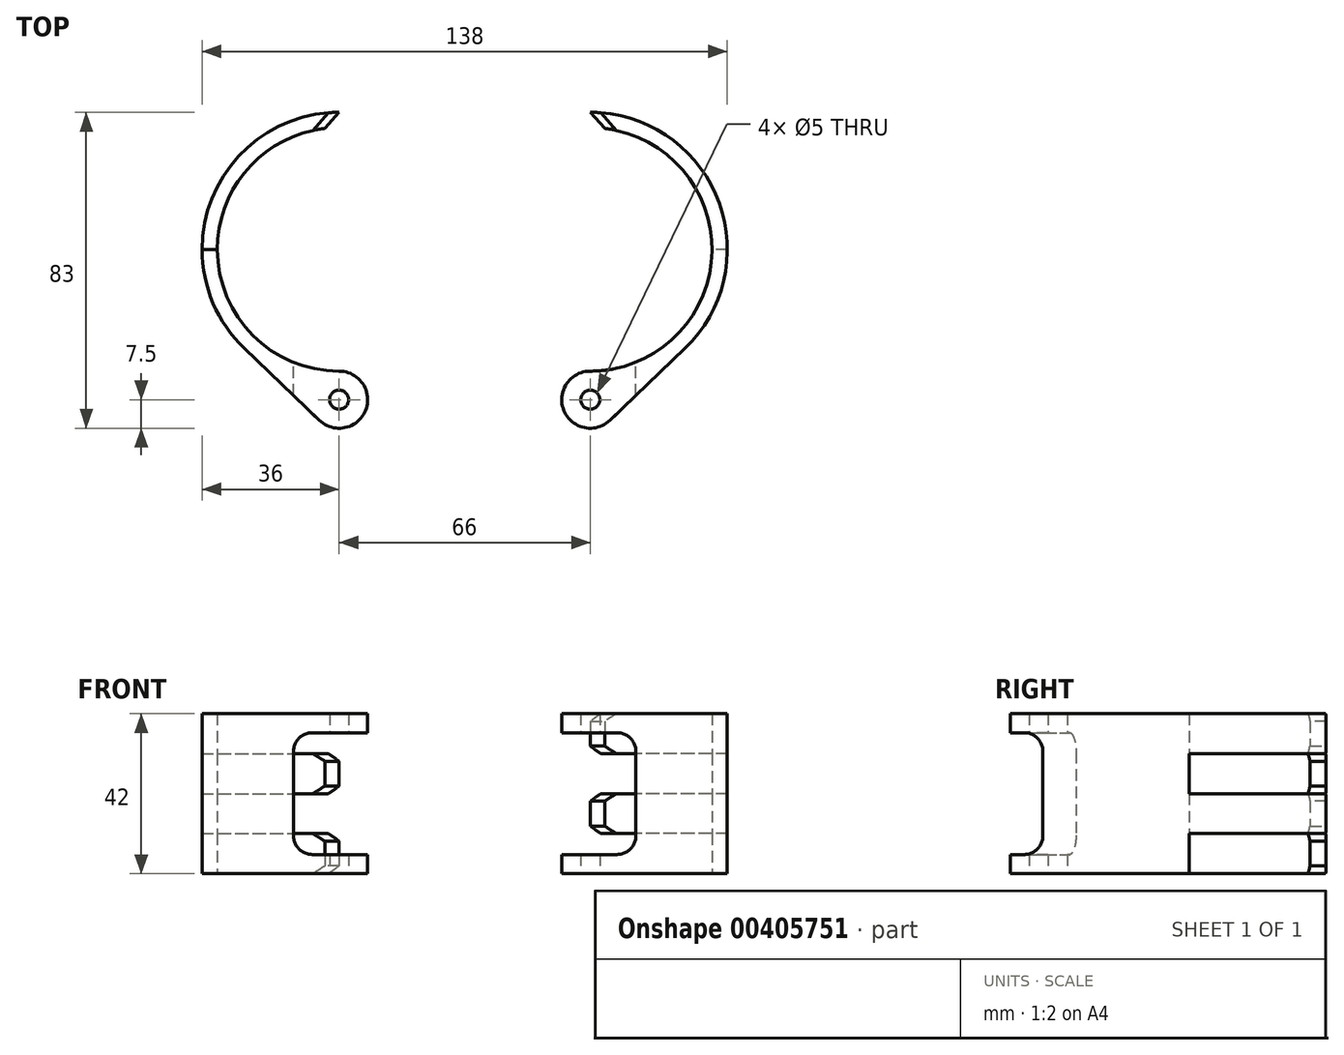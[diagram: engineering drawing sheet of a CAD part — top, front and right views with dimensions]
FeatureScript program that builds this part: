
annotation { "Feature Type Name" : "Feature", "Feature Type Description" : "" }
export const myFeature = defineFeature(function(context is Context, id is Id, definition is map)
    precondition{}
    {
        {
            var Q0;
            Q0=qCreatedBy(makeId("Top.planeOp"),FACE);
            var sketch = newSketch(context, id + "F0", { "sketchPlane" : qUnion([Q0])});
            skLineSegment(sketch, "E0", {"start": v(-33, 0) * mm, "end": v(33, 0) * mm, "construction": true});
            skPoint(sketch, "E1", {"position": v(0, 0) * mm});
            skCircle(sketch, "E2", {"center": v(-33, 0) * mm, "radius": 32 * mm});
            skCircle(sketch, "E3", {"center": v(33, 0) * mm, "radius": 32 * mm});
            skCircle(sketch, "E4", {"center": v(-33, 0) * mm, "radius": 36 * mm});
            skCircle(sketch, "E5", {"center": v(33, 0) * mm, "radius": 36 * mm});
            skCircle(sketch, "E6", {"center": v(-33, -39.5) * mm, "radius": 7.5 * mm});
            skCircle(sketch, "E7", {"center": v(33, -39.5) * mm, "radius": 7.5 * mm});
            skLineSegment(sketch, "E8", {"start": v(-38.2, -44.91) * mm, "end": v(-57.93, -25.97) * mm});
            skLineSegment(sketch, "E9", {"start": v(38.2, -44.91) * mm, "end": v(57.93, -25.97) * mm});
            skLineSegment(sketch, "E10", {"start": v(-33, 0) * mm, "end": v(-33, 36) * mm});
            skLineSegment(sketch, "E11", {"start": v(33, 0) * mm, "end": v(33, 36) * mm});
            skCircle(sketch, "E12", {"center": v(-33, -39.5) * mm, "radius": 2.5 * mm});
            skCircle(sketch, "E13", {"center": v(33, -39.5) * mm, "radius": 2.5 * mm});
            skLineSegment(sketch, "E14", {"start": v(-33, -39.5) * mm, "end": v(33, -39.5) * mm});
            skLineSegment(sketch, "E15", {"start": v(-33, 0) * mm, "end": v(-33, -39.5) * mm});
            skLineSegment(sketch, "E16", {"start": v(33, 0) * mm, "end": v(33, -39.5) * mm});
            skSolve(sketch);
        }
        {
            var Q0;
            {var subQ0=sQuery(id+"F0.wireOp",EDGE,"E6");var subQ1=sQuery(id+"F0.wireOp",EDGE,"E4");var subQ2=makeQuery(id+"F0.imprint","INTERSECT",VERTEX,{"disambiguationData":[OD(0.0)],"derivedFrom":[subQ1,subQ0]});Q0=makeQuery(id+"F0.imprint","IMPRINT",FACE,{"disambiguationData":[TD([[makeQuery(id+"F0.imprint","IMPRINT",EDGE,{"disambiguationData":[TD([[subQ2,1.0]])],"derivedFrom":subQ1}),-1.0]])]});}
            var Q1;
            {var subQ0=sQuery(id+"F0.wireOp",EDGE,"E6");var subQ1=sQuery(id+"F0.wireOp",EDGE,"E4");var subQ2=makeQuery(id+"F0.imprint","INTERSECT",VERTEX,{"disambiguationData":[OD(0.0)],"derivedFrom":[subQ1,subQ0]});Q1=makeQuery(id+"F0.imprint","IMPRINT",FACE,{"disambiguationData":[TD([[makeQuery(id+"F0.imprint","IMPRINT",EDGE,{"disambiguationData":[TD([[subQ2,1.0]])],"derivedFrom":subQ1}),1.0]])]});}
            var Q2;
            {var subQ0=sQuery(id+"F0.wireOp",EDGE,"E8");Q2=makeQuery(id+"F0.imprint","IMPRINT",FACE,{"disambiguationData":[TD([[makeQuery(id+"F0.imprint","IMPRINT",EDGE,{"derivedFrom":subQ0}),-1.0]])]});}
            var Q3;
            {var subQ0=sQuery(id+"F0.wireOp",EDGE,"E7");var subQ1=sQuery(id+"F0.wireOp",EDGE,"E5");var subQ2=makeQuery(id+"F0.imprint","INTERSECT",VERTEX,{"disambiguationData":[OD(0.0)],"derivedFrom":[subQ1,subQ0]});Q3=makeQuery(id+"F0.imprint","IMPRINT",FACE,{"disambiguationData":[TD([[makeQuery(id+"F0.imprint","IMPRINT",EDGE,{"disambiguationData":[TD([[subQ2,-1.0]])],"derivedFrom":subQ1}),-1.0]])]});}
            var Q4;
            {var subQ0=sQuery(id+"F0.wireOp",EDGE,"E9");Q4=makeQuery(id+"F0.imprint","IMPRINT",FACE,{"disambiguationData":[TD([[makeQuery(id+"F0.imprint","IMPRINT",EDGE,{"derivedFrom":subQ0}),1.0]])]});}
            var Q5;
            {var subQ0=sQuery(id+"F0.wireOp",EDGE,"E7");var subQ1=sQuery(id+"F0.wireOp",EDGE,"E5");var subQ2=makeQuery(id+"F0.imprint","INTERSECT",VERTEX,{"disambiguationData":[OD(0.0)],"derivedFrom":[subQ1,subQ0]});Q5=makeQuery(id+"F0.imprint","IMPRINT",FACE,{"disambiguationData":[TD([[makeQuery(id+"F0.imprint","IMPRINT",EDGE,{"disambiguationData":[TD([[subQ2,-1.0]])],"derivedFrom":subQ1}),1.0]])]});}
            var Q6;
            {var subQ1=sQuery(id+"F0.wireOp",EDGE,"E3");var subQ6=sQuery(id+"F0.wireOp",EDGE,"E11");var subQ8=makeQuery(id+"F0.imprint","INTERSECT",VERTEX,{"derivedFrom":[subQ1,subQ6]});Q6=makeQuery(id+"F0.imprint","IMPRINT",FACE,{"disambiguationData":[TD([[makeQuery(id+"F0.imprint","IMPRINT",EDGE,{"disambiguationData":[TD([[subQ8,1.0]])],"derivedFrom":subQ1}),-1.0]])]});}
            var Q7;
            {var subQ1=sQuery(id+"F0.wireOp",EDGE,"E2");var subQ6=sQuery(id+"F0.wireOp",EDGE,"E10");var subQ8=makeQuery(id+"F0.imprint","INTERSECT",VERTEX,{"derivedFrom":[subQ1,subQ6]});Q7=makeQuery(id+"F0.imprint","IMPRINT",FACE,{"disambiguationData":[TD([[makeQuery(id+"F0.imprint","IMPRINT",EDGE,{"disambiguationData":[TD([[subQ8,-1.0]])],"derivedFrom":subQ1}),-1.0]])]});}
            var Q8;
            Q8=makeQuery(id+"F0.imprint","IMPRINT",FACE,{"disambiguationData":[TD([[makeQuery(id+"F0.imprint","IMPRINT",EDGE,{"derivedFrom":sQuery(id+"F0.wireOp",EDGE,"E12")}),-1.0]])]});
            var Q9;
            {var subQ0=sQuery(id+"F0.wireOp",EDGE,"E6");var subQ1=sQuery(id+"F0.wireOp",EDGE,"E4");var subQ2=makeQuery(id+"F0.imprint","INTERSECT",VERTEX,{"disambiguationData":[OD(0.0)],"derivedFrom":[subQ1,subQ0]});Q9=makeQuery(id+"F0.imprint","IMPRINT",FACE,{"disambiguationData":[TD([[makeQuery(id+"F0.imprint","IMPRINT",EDGE,{"disambiguationData":[TD([[subQ2,-1.0]])],"derivedFrom":subQ1}),1.0]])]});}
            var Q10;
            {var subQ0=sQuery(id+"F0.wireOp",EDGE,"E15");var subQ1=sQuery(id+"F0.wireOp",EDGE,"E4");var subQ2=makeQuery(id+"F0.imprint","INTERSECT",VERTEX,{"derivedFrom":[subQ1,subQ0]});Q10=makeQuery(id+"F0.imprint","IMPRINT",FACE,{"disambiguationData":[TD([[makeQuery(id+"F0.imprint","IMPRINT",EDGE,{"disambiguationData":[TD([[subQ2,-1.0]])],"derivedFrom":subQ1}),1.0]])]});}
            var Q11;
            {var subQ5=sQuery(id+"F0.wireOp",EDGE,"E6");var subQ8=sQuery(id+"F0.wireOp",EDGE,"E4");var subQ9=makeQuery(id+"F0.imprint","INTERSECT",VERTEX,{"disambiguationData":[OD(0.0)],"derivedFrom":[subQ8,subQ5]});Q11=makeQuery(id+"F0.imprint","IMPRINT",FACE,{"disambiguationData":[TD([[makeQuery(id+"F0.imprint","IMPRINT",EDGE,{"disambiguationData":[TD([[subQ9,-1.0]])],"derivedFrom":subQ8}),-1.0]])]});}
            var Q12;
            {var subQ3=sQuery(id+"F0.wireOp",EDGE,"E16");var subQ8=sQuery(id+"F0.wireOp",EDGE,"E5");var subQ9=makeQuery(id+"F0.imprint","INTERSECT",VERTEX,{"derivedFrom":[subQ8,subQ3]});Q12=makeQuery(id+"F0.imprint","IMPRINT",FACE,{"disambiguationData":[TD([[makeQuery(id+"F0.imprint","IMPRINT",EDGE,{"disambiguationData":[TD([[subQ9,-1.0]])],"derivedFrom":subQ8}),-1.0]])]});}
            var Q13;
            {var subQ0=sQuery(id+"F0.wireOp",EDGE,"E16");var subQ1=sQuery(id+"F0.wireOp",EDGE,"E5");var subQ2=makeQuery(id+"F0.imprint","INTERSECT",VERTEX,{"derivedFrom":[subQ1,subQ0]});Q13=makeQuery(id+"F0.imprint","IMPRINT",FACE,{"disambiguationData":[TD([[makeQuery(id+"F0.imprint","IMPRINT",EDGE,{"disambiguationData":[TD([[subQ2,-1.0]])],"derivedFrom":subQ1}),1.0]])]});}
            extrude(context, id + "F1", {"entities" : qUnion([Q0, Q1, Q2, Q3, Q4, Q5, Q6, Q7, Q8, Q9, Q10, Q11, Q12, Q13]), "endBound" : BoundingType.SYMMETRIC, "depth" : 42 * mm});
        }
        {
            var Q0;
            Q0=qCreatedBy(makeId("Front.planeOp"),FACE);
            var sketch = newSketch(context, id + "F2", { "sketchPlane" : qUnion([Q0])});
            skLineSegment(sketch, "E17.bottom", {"start": v(-45, 16) * mm, "end": v(45, 16) * mm});
            skLineSegment(sketch, "E17.top", {"start": v(-45, -16) * mm, "end": v(45, -16) * mm});
            skLineSegment(sketch, "E17.left", {"start": v(-45, 16) * mm, "end": v(-45, -16) * mm});
            skLineSegment(sketch, "E17.right", {"start": v(45, 16) * mm, "end": v(45, -16) * mm});
            skLineSegment(sketch, "E18", {"start": v(-45, 16) * mm, "end": v(45, -16) * mm, "construction": true});
            skPoint(sketch, "E19", {"position": v(0, 0) * mm});
            skSolve(sketch);
        }
        {
            var Q0;
            Q0=makeQuery(id+"F2.imprint","IMPRINT",FACE,{"disambiguationData":[TD([[makeQuery(id+"F2.imprint","IMPRINT",EDGE,{"derivedFrom":sQuery(id+"F2.wireOp",EDGE,"E17.bottom")}),-1.0]])]});
            var Q1;
            Q1=makeQuery(id+"F1.opExtrude","CAP_VERTEX",VERTEX,{"disambiguationData":[OSD([sQuery(id+"F0.wireOp",EDGE,"E6"),sQuery(id+"F0.wireOp",EDGE,"E8")])],"isStart":false});
            extrude(context, id + "F3", {"entities" : qUnion([Q0]), "operationType" : NewBodyOperationType.REMOVE, "endBoundEntityVertex" : qUnion([Q1]), "depth" : 60 * mm});
        }
        {
            var Q0;
            Q0=makeQuery(id+"F3.boolean.opBoolean","COPY",EDGE,{"derivedFrom":makeQuery(id+"F3.opExtrude","SWEPT_EDGE",EDGE,{"disambiguationData":[OSD([sQuery(id+"F2.wireOp",EDGE,"E17.bottom"),sQuery(id+"F2.wireOp",EDGE,"E17.right")])]})});
            var Q1;
            Q1=makeQuery(id+"F3.boolean.opBoolean","COPY",EDGE,{"derivedFrom":makeQuery(id+"F3.opExtrude","SWEPT_EDGE",EDGE,{"disambiguationData":[OSD([sQuery(id+"F2.wireOp",EDGE,"E17.top"),sQuery(id+"F2.wireOp",EDGE,"E17.right")])]})});
            var Q2;
            Q2=makeQuery(id+"F3.boolean.opBoolean","COPY",EDGE,{"derivedFrom":makeQuery(id+"F3.opExtrude","SWEPT_EDGE",EDGE,{"disambiguationData":[OSD([sQuery(id+"F2.wireOp",EDGE,"E17.bottom"),sQuery(id+"F2.wireOp",EDGE,"E17.left")])]})});
            var Q3;
            Q3=makeQuery(id+"F3.boolean.opBoolean","COPY",EDGE,{"derivedFrom":makeQuery(id+"F3.opExtrude","SWEPT_EDGE",EDGE,{"disambiguationData":[OSD([sQuery(id+"F2.wireOp",EDGE,"E17.top"),sQuery(id+"F2.wireOp",EDGE,"E17.left")])]})});
            fillet(context, id + "F4", {"entities" : qUnion([Q0, Q1, Q2, Q3]), "radius" : 5 * mm, "tangentPropagation" : true, "allowEdgeOverflow" : false});
        }
        {
            var Q0;
            Q0=qCreatedBy(makeId("Right.planeOp"),FACE);
            var sketch = newSketch(context, id + "F5", { "sketchPlane" : qUnion([Q0])});
            skLineSegment(sketch, "E20.bottom", {"start": v(0, 0) * mm, "end": v(36, 0) * mm});
            skLineSegment(sketch, "E20.top", {"start": v(0, 10.5) * mm, "end": v(36, 10.5) * mm});
            skLineSegment(sketch, "E20.left", {"start": v(0, 0) * mm, "end": v(0, 10.5) * mm});
            skLineSegment(sketch, "E20.right", {"start": v(36, 0) * mm, "end": v(36, 10.5) * mm});
            skLineSegment(sketch, "E21.top", {"start": v(0, 21) * mm, "end": v(36, 21) * mm});
            skLineSegment(sketch, "E21.left", {"start": v(0, 10.5) * mm, "end": v(0, 21) * mm});
            skLineSegment(sketch, "E21.right", {"start": v(36, 10.5) * mm, "end": v(36, 21) * mm});
            skLineSegment(sketch, "E22.top", {"start": v(0, -10.5) * mm, "end": v(36, -10.5) * mm});
            skLineSegment(sketch, "E22.left", {"start": v(0, 0) * mm, "end": v(0, -10.5) * mm});
            skLineSegment(sketch, "E22.right", {"start": v(36, 0) * mm, "end": v(36, -10.5) * mm});
            skLineSegment(sketch, "E23.top", {"start": v(0, -21) * mm, "end": v(36, -21) * mm});
            skLineSegment(sketch, "E23.left", {"start": v(0, -10.5) * mm, "end": v(0, -21) * mm});
            skLineSegment(sketch, "E23.right", {"start": v(36, -10.5) * mm, "end": v(36, -21) * mm});
            skSolve(sketch);
        }
        {
            var Q0;
            Q0=makeQuery(id+"F5.imprint","IMPRINT",FACE,{"disambiguationData":[TD([[makeQuery(id+"F5.imprint","IMPRINT",EDGE,{"derivedFrom":sQuery(id+"F5.wireOp",EDGE,"E20.top")}),1.0]])]});
            var Q1;
            Q1=makeQuery(id+"F5.imprint","IMPRINT",FACE,{"disambiguationData":[TD([[makeQuery(id+"F5.imprint","IMPRINT",EDGE,{"derivedFrom":sQuery(id+"F5.wireOp",EDGE,"E20.bottom")}),-1.0]])]});
            extrude(context, id + "F6", {"entities" : qUnion([Q0, Q1]), "operationType" : NewBodyOperationType.REMOVE, "oppositeDirection" : true, "depth" : 80 * mm});
        }
        {
            var Q0;
            Q0=qCreatedBy(makeId("Right.planeOp"),FACE);
            var sketch = newSketch(context, id + "F7", { "sketchPlane" : qUnion([Q0])});
            skLineSegment(sketch, "E24.bottom", {"start": v(0, 0) * mm, "end": v(36, 0) * mm});
            skLineSegment(sketch, "E24.top", {"start": v(0, 10.5) * mm, "end": v(36, 10.5) * mm});
            skLineSegment(sketch, "E24.left", {"start": v(0, 0) * mm, "end": v(0, 10.5) * mm});
            skLineSegment(sketch, "E24.right", {"start": v(36, 0) * mm, "end": v(36, 10.5) * mm});
            skLineSegment(sketch, "E25.top", {"start": v(0, 21) * mm, "end": v(36, 21) * mm});
            skLineSegment(sketch, "E25.left", {"start": v(0, 10.5) * mm, "end": v(0, 21) * mm});
            skLineSegment(sketch, "E25.right", {"start": v(36, 10.5) * mm, "end": v(36, 21) * mm});
            skLineSegment(sketch, "E26.top", {"start": v(0, -10.5) * mm, "end": v(36, -10.5) * mm});
            skLineSegment(sketch, "E26.left", {"start": v(0, 0) * mm, "end": v(0, -10.5) * mm});
            skLineSegment(sketch, "E26.right", {"start": v(36, 0) * mm, "end": v(36, -10.5) * mm});
            skLineSegment(sketch, "E27.top", {"start": v(0, -21) * mm, "end": v(36, -21) * mm});
            skLineSegment(sketch, "E27.left", {"start": v(0, -10.5) * mm, "end": v(0, -21) * mm});
            skLineSegment(sketch, "E27.right", {"start": v(36, -10.5) * mm, "end": v(36, -21) * mm});
            skSolve(sketch);
        }
        {
            var Q0;
            Q0=makeQuery(id+"F7.imprint","IMPRINT",FACE,{"disambiguationData":[TD([[makeQuery(id+"F7.imprint","IMPRINT",EDGE,{"derivedFrom":sQuery(id+"F7.wireOp",EDGE,"E24.left")}),-1.0]])]});
            var Q1;
            Q1=makeQuery(id+"F7.imprint","IMPRINT",FACE,{"disambiguationData":[TD([[makeQuery(id+"F7.imprint","IMPRINT",EDGE,{"derivedFrom":sQuery(id+"F7.wireOp",EDGE,"E26.top")}),-1.0]])]});
            extrude(context, id + "F8", {"entities" : qUnion([Q0, Q1]), "operationType" : NewBodyOperationType.REMOVE, "depth" : 80 * mm});
        }
        {
            var Q0;
            {var subQ0=sQuery(id+"F0.wireOp",EDGE,"E2");var subQ1=sQuery(id+"F0.wireOp",EDGE,"E10");Q0=makeQuery(id+"F6.boolean.opBoolean","SPLIT",EDGE,{"disambiguationData":[TD([makeQuery(id+"F6.opExtrude","SWEPT_FACE",FACE,{"disambiguationData":[OSD([sQuery(id+"F5.wireOp",EDGE,"E20.top")])]})])],"derivedFrom":makeQuery(id+"F1.opExtrude","SWEPT_EDGE",EDGE,{"disambiguationData":[OSD([subQ0,subQ1])]})});}
            var Q1;
            {var subQ0=sQuery(id+"F0.wireOp",EDGE,"E2");var subQ1=sQuery(id+"F0.wireOp",EDGE,"E10");Q1=makeQuery(id+"F6.boolean.opBoolean","SPLIT",EDGE,{"disambiguationData":[TD([makeQuery(id+"F6.opExtrude","SWEPT_FACE",FACE,{"disambiguationData":[OSD([sQuery(id+"F5.wireOp",EDGE,"E22.top")])]})])],"derivedFrom":makeQuery(id+"F1.opExtrude","SWEPT_EDGE",EDGE,{"disambiguationData":[OSD([subQ0,subQ1])]})});}
            var Q2;
            {var subQ0=sQuery(id+"F0.wireOp",EDGE,"E3");var subQ1=sQuery(id+"F0.wireOp",EDGE,"E11");Q2=makeQuery(id+"F8.boolean.opBoolean","SPLIT",EDGE,{"disambiguationData":[TD([makeQuery(id+"F8.opExtrude","SWEPT_FACE",FACE,{"disambiguationData":[OSD([sQuery(id+"F7.wireOp",EDGE,"E24.top")])]})])],"derivedFrom":makeQuery(id+"F1.opExtrude","SWEPT_EDGE",EDGE,{"disambiguationData":[OSD([subQ0,subQ1])]})});}
            var Q3;
            {var subQ0=sQuery(id+"F0.wireOp",EDGE,"E3");var subQ1=sQuery(id+"F0.wireOp",EDGE,"E11");Q3=makeQuery(id+"F8.boolean.opBoolean","SPLIT",EDGE,{"disambiguationData":[TD([makeQuery(id+"F8.opExtrude","SWEPT_FACE",FACE,{"disambiguationData":[OSD([sQuery(id+"F7.wireOp",EDGE,"E24.bottom")])]})])],"derivedFrom":makeQuery(id+"F1.opExtrude","SWEPT_EDGE",EDGE,{"disambiguationData":[OSD([subQ0,subQ1])]})});}
            chamfer(context, id + "F9", {"entities" : qUnion([Q0, Q1, Q2, Q3]), "width" : 4.25 * mm, "tangentPropagation" : true});
        }
        {
            var Q0;
            {var subQ0=makeQuery(id+"F6.opExtrude","SWEPT_FACE",FACE,{"disambiguationData":[OSD([sQuery(id+"F5.wireOp",EDGE,"E20.top")])]});var subQ1=sQuery(id+"F0.wireOp",EDGE,"E2");var subQ2=sQuery(id+"F0.wireOp",EDGE,"E10");Q0=makeQuery(id+"F9.opChamfer","BLEND_EDGE",EDGE,{"blendedFrom":[makeQuery(id+"F6.boolean.opBoolean","SPLIT",EDGE,{"disambiguationData":[TD([subQ0])],"derivedFrom":makeQuery(id+"F1.opExtrude","SWEPT_EDGE",EDGE,{"disambiguationData":[OSD([subQ1,subQ2])]})}),makeQuery(id+"F6.boolean.opBoolean","COPY",FACE,{"derivedFrom":subQ0})],"blendedInto":[makeQuery(id+"F6.boolean.opBoolean","COPY",FACE,{"derivedFrom":subQ0})]});}
            var Q1;
            {var subQ0=makeQuery(id+"F6.opExtrude","SWEPT_FACE",FACE,{"disambiguationData":[OSD([sQuery(id+"F5.wireOp",EDGE,"E22.top")])]});var subQ1=sQuery(id+"F0.wireOp",EDGE,"E2");var subQ2=sQuery(id+"F0.wireOp",EDGE,"E10");Q1=makeQuery(id+"F9.opChamfer","BLEND_EDGE",EDGE,{"blendedFrom":[makeQuery(id+"F6.boolean.opBoolean","SPLIT",EDGE,{"disambiguationData":[TD([subQ0])],"derivedFrom":makeQuery(id+"F1.opExtrude","SWEPT_EDGE",EDGE,{"disambiguationData":[OSD([subQ1,subQ2])]})}),makeQuery(id+"F6.boolean.opBoolean","COPY",FACE,{"derivedFrom":subQ0})],"blendedInto":[makeQuery(id+"F6.boolean.opBoolean","COPY",FACE,{"derivedFrom":subQ0})]});}
            var Q2;
            {var subQ0=makeQuery(id+"F8.opExtrude","SWEPT_FACE",FACE,{"disambiguationData":[OSD([sQuery(id+"F7.wireOp",EDGE,"E26.top")])]});var subQ1=sQuery(id+"F0.wireOp",EDGE,"E3");var subQ2=sQuery(id+"F0.wireOp",EDGE,"E11");Q2=makeQuery(id+"F9.opChamfer","BLEND_EDGE",EDGE,{"blendedFrom":[makeQuery(id+"F8.boolean.opBoolean","SPLIT",EDGE,{"disambiguationData":[TD([makeQuery(id+"F8.opExtrude","SWEPT_FACE",FACE,{"disambiguationData":[OSD([sQuery(id+"F7.wireOp",EDGE,"E24.bottom")])]})])],"derivedFrom":makeQuery(id+"F1.opExtrude","SWEPT_EDGE",EDGE,{"disambiguationData":[OSD([subQ1,subQ2])]})}),makeQuery(id+"F8.boolean.opBoolean","COPY",FACE,{"derivedFrom":subQ0})],"blendedInto":[makeQuery(id+"F8.boolean.opBoolean","COPY",FACE,{"derivedFrom":subQ0})]});}
            var Q3;
            {var subQ0=makeQuery(id+"F8.opExtrude","SWEPT_FACE",FACE,{"disambiguationData":[OSD([sQuery(id+"F7.wireOp",EDGE,"E24.top")])]});var subQ1=sQuery(id+"F0.wireOp",EDGE,"E3");var subQ2=sQuery(id+"F0.wireOp",EDGE,"E11");Q3=makeQuery(id+"F9.opChamfer","BLEND_EDGE",EDGE,{"blendedFrom":[makeQuery(id+"F8.boolean.opBoolean","SPLIT",EDGE,{"disambiguationData":[TD([subQ0])],"derivedFrom":makeQuery(id+"F1.opExtrude","SWEPT_EDGE",EDGE,{"disambiguationData":[OSD([subQ1,subQ2])]})}),makeQuery(id+"F8.boolean.opBoolean","COPY",FACE,{"derivedFrom":subQ0})],"blendedInto":[makeQuery(id+"F8.boolean.opBoolean","COPY",FACE,{"derivedFrom":subQ0})]});}
            var Q4;
            {var subQ0=sQuery(id+"F0.wireOp",EDGE,"E10");var subQ1=sQuery(id+"F0.wireOp",EDGE,"E2");var subQ2=makeQuery(id+"F1.opExtrude","CAP_FACE",FACE,{"disambiguationData":[OSD([subQ1,sQuery(id+"F0.wireOp",EDGE,"E4"),sQuery(id+"F0.wireOp",EDGE,"E6"),sQuery(id+"F0.wireOp",EDGE,"E8"),subQ0,sQuery(id+"F0.wireOp",EDGE,"E12")])],"isStart":true});Q4=makeQuery(id+"F9.opChamfer","BLEND_EDGE",EDGE,{"blendedFrom":[makeQuery(id+"F6.boolean.opBoolean","SPLIT",EDGE,{"disambiguationData":[TD([makeQuery(id+"F6.opExtrude","SWEPT_FACE",FACE,{"disambiguationData":[OSD([sQuery(id+"F5.wireOp",EDGE,"E22.top")])]})])],"derivedFrom":makeQuery(id+"F1.opExtrude","SWEPT_EDGE",EDGE,{"disambiguationData":[OSD([subQ1,subQ0])]})}),subQ2],"blendedInto":[subQ2]});}
            var Q5;
            {var subQ0=makeQuery(id+"F6.opExtrude","SWEPT_FACE",FACE,{"disambiguationData":[OSD([sQuery(id+"F5.wireOp",EDGE,"E20.bottom")])]});var subQ1=sQuery(id+"F0.wireOp",EDGE,"E2");var subQ2=sQuery(id+"F0.wireOp",EDGE,"E10");Q5=makeQuery(id+"F9.opChamfer","BLEND_EDGE",EDGE,{"blendedFrom":[makeQuery(id+"F6.boolean.opBoolean","SPLIT",EDGE,{"disambiguationData":[TD([makeQuery(id+"F6.opExtrude","SWEPT_FACE",FACE,{"disambiguationData":[OSD([sQuery(id+"F5.wireOp",EDGE,"E20.top")])]})])],"derivedFrom":makeQuery(id+"F1.opExtrude","SWEPT_EDGE",EDGE,{"disambiguationData":[OSD([subQ1,subQ2])]})}),makeQuery(id+"F6.boolean.opBoolean","COPY",FACE,{"derivedFrom":subQ0})],"blendedInto":[makeQuery(id+"F6.boolean.opBoolean","COPY",FACE,{"derivedFrom":subQ0})]});}
            var Q6;
            {var subQ0=sQuery(id+"F0.wireOp",EDGE,"E11");var subQ1=sQuery(id+"F0.wireOp",EDGE,"E3");var subQ2=makeQuery(id+"F1.opExtrude","CAP_FACE",FACE,{"disambiguationData":[OSD([subQ1,sQuery(id+"F0.wireOp",EDGE,"E5"),sQuery(id+"F0.wireOp",EDGE,"E7"),sQuery(id+"F0.wireOp",EDGE,"E9"),subQ0,sQuery(id+"F0.wireOp",EDGE,"E13")])],"isStart":false});Q6=makeQuery(id+"F9.opChamfer","BLEND_EDGE",EDGE,{"blendedFrom":[makeQuery(id+"F8.boolean.opBoolean","SPLIT",EDGE,{"disambiguationData":[TD([makeQuery(id+"F8.opExtrude","SWEPT_FACE",FACE,{"disambiguationData":[OSD([sQuery(id+"F7.wireOp",EDGE,"E24.top")])]})])],"derivedFrom":makeQuery(id+"F1.opExtrude","SWEPT_EDGE",EDGE,{"disambiguationData":[OSD([subQ1,subQ0])]})}),subQ2],"blendedInto":[subQ2]});}
            var Q7;
            {var subQ0=makeQuery(id+"F8.opExtrude","SWEPT_FACE",FACE,{"disambiguationData":[OSD([sQuery(id+"F7.wireOp",EDGE,"E24.bottom")])]});var subQ1=sQuery(id+"F0.wireOp",EDGE,"E3");var subQ2=sQuery(id+"F0.wireOp",EDGE,"E11");Q7=makeQuery(id+"F9.opChamfer","BLEND_EDGE",EDGE,{"blendedFrom":[makeQuery(id+"F8.boolean.opBoolean","SPLIT",EDGE,{"disambiguationData":[TD([subQ0])],"derivedFrom":makeQuery(id+"F1.opExtrude","SWEPT_EDGE",EDGE,{"disambiguationData":[OSD([subQ1,subQ2])]})}),makeQuery(id+"F8.boolean.opBoolean","COPY",FACE,{"derivedFrom":subQ0})],"blendedInto":[makeQuery(id+"F8.boolean.opBoolean","COPY",FACE,{"derivedFrom":subQ0})]});}
            chamfer(context, id + "F10", {"entities" : qUnion([Q0, Q1, Q2, Q3, Q4, Q5, Q6, Q7]), "width" : 2 * mm, "tangentPropagation" : true});
        }
    });
